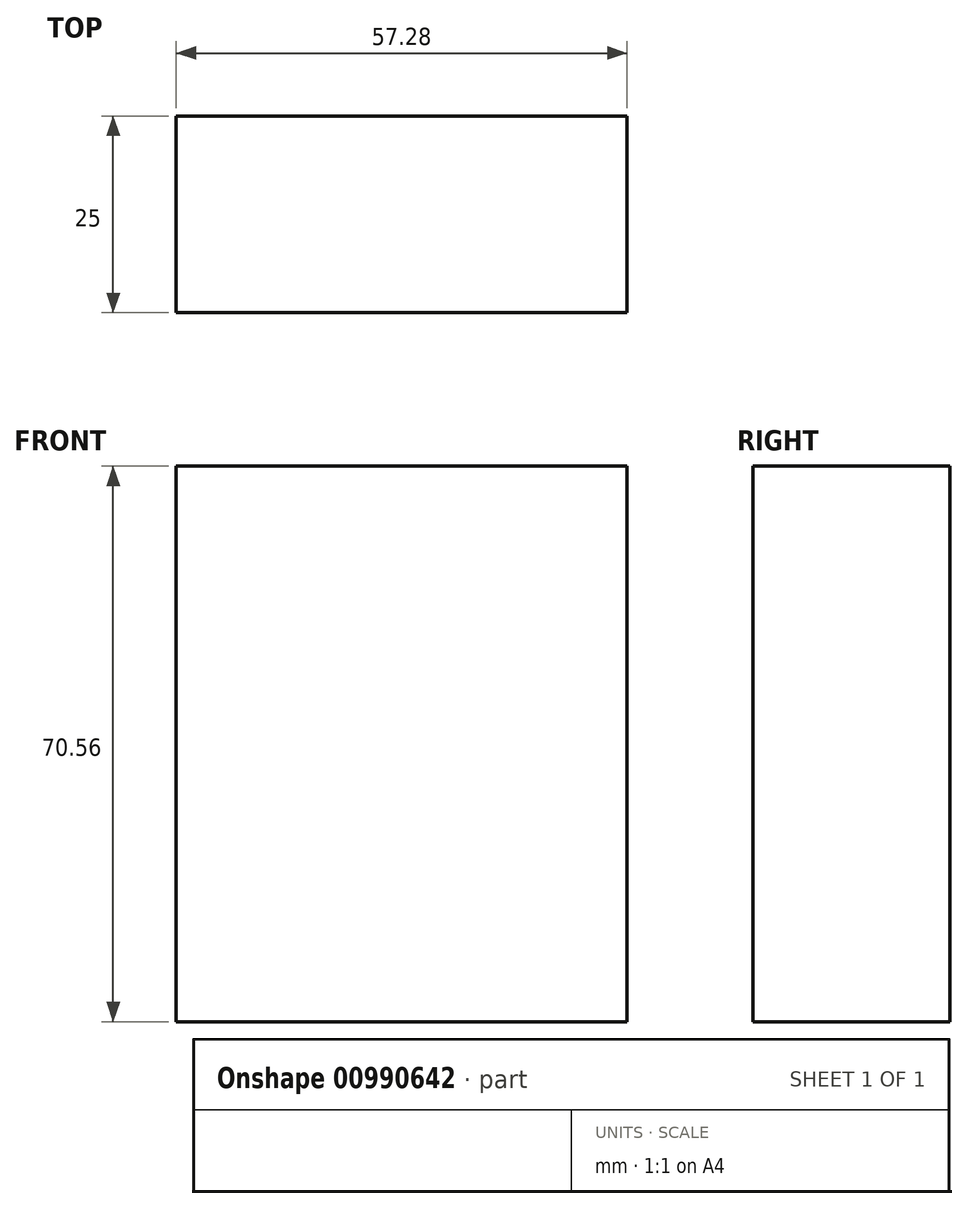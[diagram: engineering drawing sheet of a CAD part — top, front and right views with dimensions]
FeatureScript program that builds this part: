
annotation { "Feature Type Name" : "Feature", "Feature Type Description" : "" }
export const myFeature = defineFeature(function(context is Context, id is Id, definition is map)
    precondition{}
    {
        {
            var Q0;
            Q0=qCreatedBy(makeId("Front.planeOp"),FACE);
            var sketch = newSketch(context, id + "F0", { "sketchPlane" : qUnion([Q0])});
            skLineSegment(sketch, "E0.bottom", {"start": v(-124.35, 10.72) * mm, "end": v(-67.07, 10.72) * mm});
            skLineSegment(sketch, "E0.top", {"start": v(-124.35, -59.84) * mm, "end": v(-67.07, -59.84) * mm});
            skLineSegment(sketch, "E0.left", {"start": v(-124.35, 10.72) * mm, "end": v(-124.35, -59.84) * mm});
            skLineSegment(sketch, "E0.right", {"start": v(-67.07, 10.72) * mm, "end": v(-67.07, -59.84) * mm});
            skSolve(sketch);
        }
        {
            var Q0;
            Q0 = qSketchRegion(id + "F0", true);
            var Q1;
            Q1 = qConstructionFilter(qBodyType(qCreatedBy(id + "F0" ,EDGE), BodyType.WIRE), ConstructionObject.NO);
            extrude(context, id + "F1", {"entities" : qUnion([Q0]), "bodyType" : ToolBodyType.SURFACE, "surfaceEntities" : qUnion([Q1]), "depth" : 25 * mm, "offsetDistance" : 25 * mm});
        }
    });
